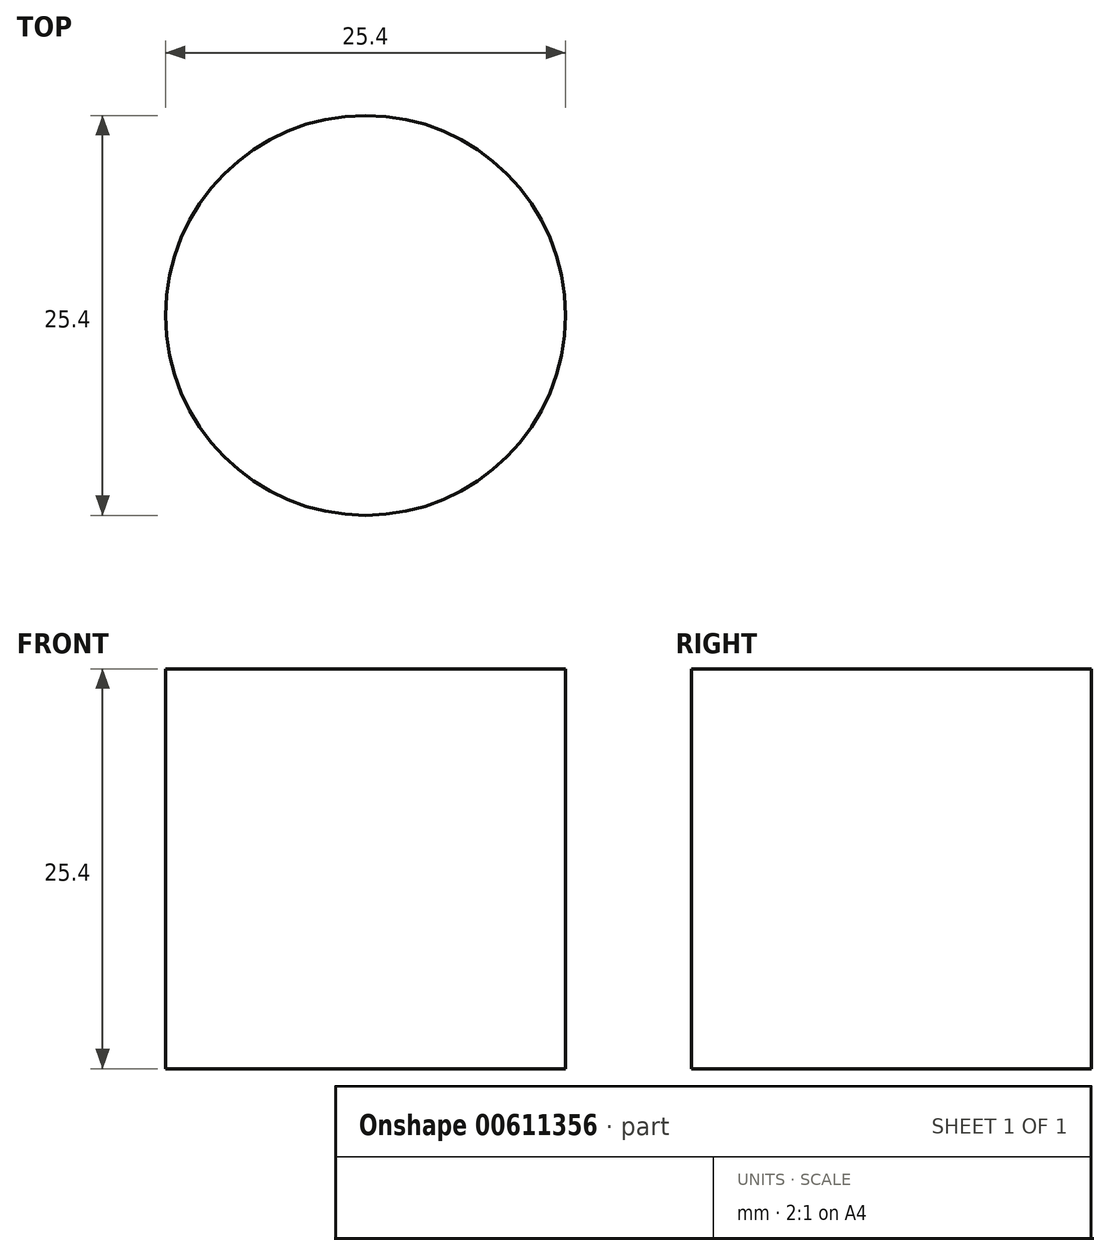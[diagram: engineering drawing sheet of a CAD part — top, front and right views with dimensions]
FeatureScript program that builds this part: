
annotation { "Feature Type Name" : "Feature", "Feature Type Description" : "" }
export const myFeature = defineFeature(function(context is Context, id is Id, definition is map)
    precondition{}
    {
        {
            var Q0;
            Q0=qCreatedBy(makeId("Top.planeOp"),FACE);
            var sketch = newSketch(context, id + "F0", { "sketchPlane" : qUnion([Q0])});
            skCircle(sketch, "E0", {"center": v(0, 0) * mm, "radius": 12.7 * mm});
            skLineSegment(sketch, "E1", {"start": v(0, 0) * mm, "end": v(0, 22.85) * mm, "construction": true});
            skLineSegment(sketch, "E2", {"start": v(-11.43, 12.7) * mm, "end": v(11.43, 12.7) * mm, "construction": true});
            skPoint(sketch, "E3", {"position": v(0, 12.7) * mm});
            skLineSegment(sketch, "E4", {"start": v(-10.47, 8.89) * mm, "end": v(10.47, 16.51) * mm, "construction": true});
            skLineSegment(sketch, "E5", {"start": v(0, 0) * mm, "end": v(-4.08, 11.21) * mm, "construction": true});
            skSolve(sketch);
        }
        {
            var Q0;
            Q0=makeQuery(id+"F0.imprint","IMPRINT",FACE,{"disambiguationData":[TD([[makeQuery(id+"F0.imprint","IMPRINT",EDGE,{"derivedFrom":sQuery(id+"F0.wireOp",EDGE,"E0")}),1.0]])]});
            extrude(context, id + "F1", {"entities" : qUnion([Q0]), "depth" : 25.4 * mm, "offsetDistance" : 25.4 * mm});
        }
    });
